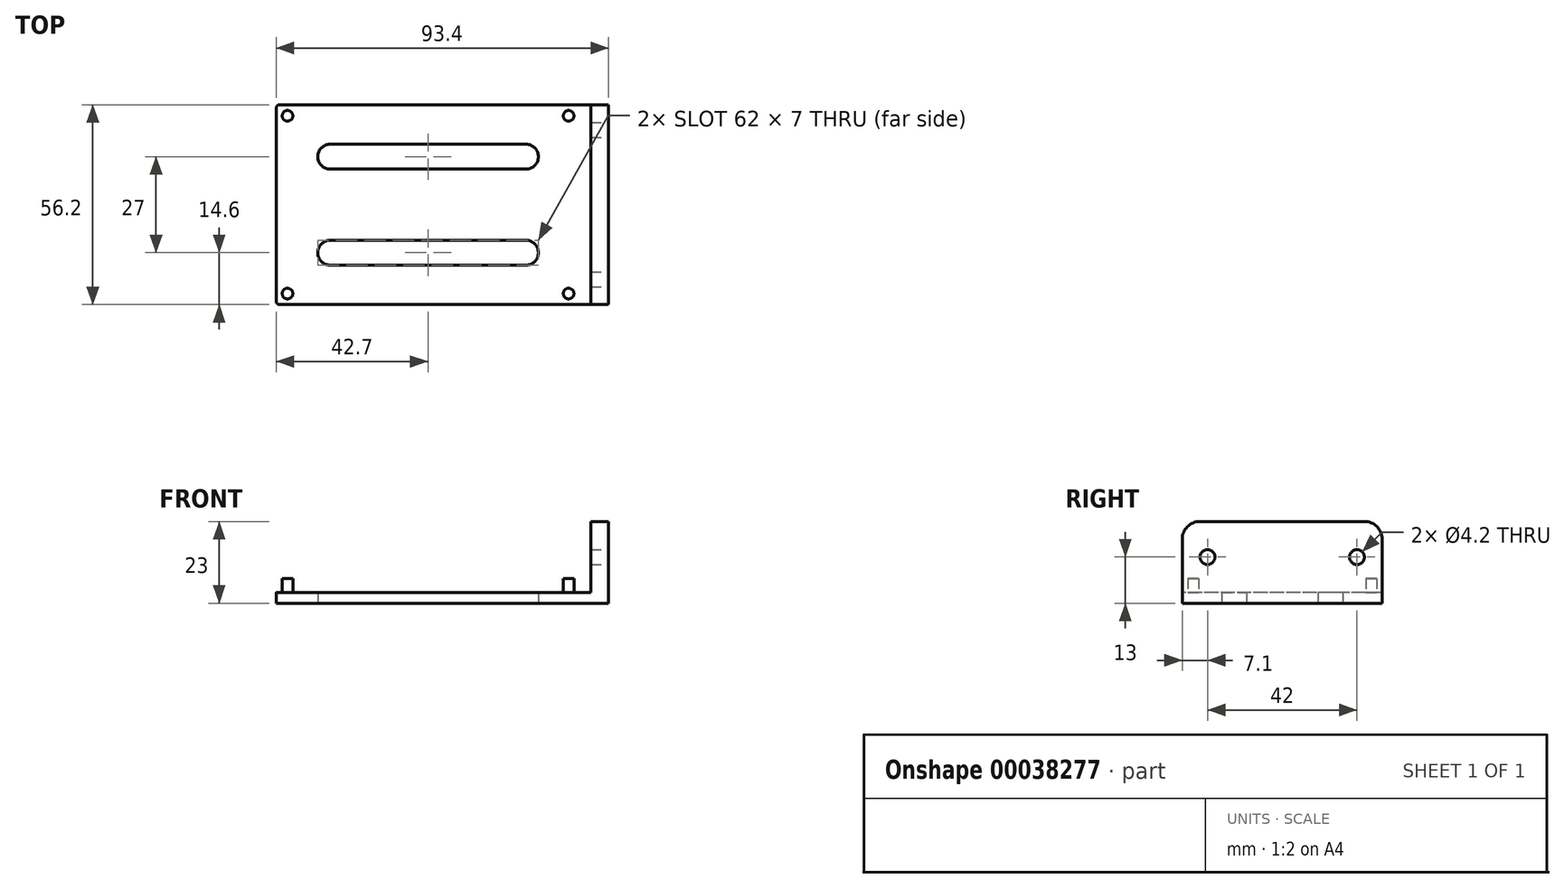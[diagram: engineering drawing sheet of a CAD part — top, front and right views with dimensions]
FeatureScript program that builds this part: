
annotation { "Feature Type Name" : "Feature", "Feature Type Description" : "" }
export const myFeature = defineFeature(function(context is Context, id is Id, definition is map)
    precondition{}
    {
        {
            var Q0;
            Q0=qCreatedBy(makeId("Top.planeOp"),FACE);
            var sketch = newSketch(context, id + "F0", { "sketchPlane" : qUnion([Q0])});
            skArc(sketch, "E0", {"start": v(-41.7, 28.1) * mm, "mid": v(-42.4, 27.8) * mm, "end": v(-42.7, 27.1) * mm});
            skLineSegment(sketch, "E1", {"start": v(-42.7, 27.1) * mm, "end": v(-42.7, -27.1) * mm});
            skArc(sketch, "E2", {"start": v(42.7, 27.1) * mm, "mid": v(42.4, 27.8) * mm, "end": v(41.7, 28.1) * mm});
            skArc(sketch, "E3", {"start": v(41.7, -28.1) * mm, "mid": v(42.4, -27.8) * mm, "end": v(42.7, -27.1) * mm});
            skLineSegment(sketch, "E4", {"start": v(42.7, -27.1) * mm, "end": v(42.7, 27.1) * mm});
            skArc(sketch, "E5", {"start": v(-42.7, -27.1) * mm, "mid": v(-42.4, -27.8) * mm, "end": v(-41.7, -28.1) * mm});
            skLineSegment(sketch, "E6", {"start": v(-41.7, -28.1) * mm, "end": v(41.7, -28.1) * mm});
            skCircle(sketch, "E7", {"center": v(39.5, 25) * mm, "radius": 1.5 * mm});
            skCircle(sketch, "E8", {"center": v(39.5, -25) * mm, "radius": 1.5 * mm});
            skCircle(sketch, "E9", {"center": v(-39.5, -25) * mm, "radius": 1.5 * mm});
            skCircle(sketch, "E10", {"center": v(-39.5, 25) * mm, "radius": 1.5 * mm});
            skCircle(sketch, "E11", {"center": v(-39.5, 25) * mm, "radius": 3.1 * mm});
            skLineSegment(sketch, "E12.bottom", {"start": v(-27.5, 17) * mm, "end": v(27.5, 17) * mm});
            skLineSegment(sketch, "E12.top", {"start": v(-27.5, 10) * mm, "end": v(27.5, 10) * mm});
            skLineSegment(sketch, "E12.left", {"start": v(-27.5, 17) * mm, "end": v(-27.5, 10) * mm, "construction": true});
            skLineSegment(sketch, "E12.right", {"start": v(27.5, 17) * mm, "end": v(27.5, 10) * mm, "construction": true});
            skArc(sketch, "E13", {"start": v(-27.5, 17) * mm, "mid": v(-31, 13.5) * mm, "end": v(-27.5, 10) * mm});
            skArc(sketch, "E14", {"start": v(27.5, 10) * mm, "mid": v(31, 13.5) * mm, "end": v(27.5, 17) * mm});
            skLineSegment(sketch, "E15", {"start": v(-42.7, 0) * mm, "end": v(42.7, 0) * mm, "construction": true});
            skLineSegment(sketch, "E16.MirrorCS", {"start": v(-27.5, -17) * mm, "end": v(-27.5, -10) * mm});
            skLineSegment(sketch, "E17.MirrorCS", {"start": v(27.5, -17) * mm, "end": v(27.5, -10) * mm});
            skArc(sketch, "E18.MirrorCS", {"start": v(27.5, -10) * mm, "mid": v(31, -13.5) * mm, "end": v(27.5, -17) * mm});
            skLineSegment(sketch, "E19.MirrorCS", {"start": v(-27.5, -10) * mm, "end": v(27.5, -10) * mm});
            skLineSegment(sketch, "E20.MirrorCS", {"start": v(-27.5, -17) * mm, "end": v(27.5, -17) * mm});
            skArc(sketch, "E21.MirrorCS", {"start": v(-27.5, -17) * mm, "mid": v(-31, -13.5) * mm, "end": v(-27.5, -10) * mm});
            skLineSegment(sketch, "E22", {"start": v(0, 17) * mm, "end": v(0, 10) * mm, "construction": true});
            skCircle(sketch, "E23.MirrorC", {"center": v(-39.5, -25) * mm, "radius": 3.1 * mm});
            skCircle(sketch, "E24.MirrorC", {"center": v(39.5, 25) * mm, "radius": 3.1 * mm});
            skCircle(sketch, "E25.MirrorC", {"center": v(39.5, -25) * mm, "radius": 3.1 * mm});
            skLineSegment(sketch, "E26", {"start": v(41.7, 28.1) * mm, "end": v(-41.7, 28.1) * mm});
            skLineSegment(sketch, "E27.bottom", {"start": v(41.7, 28.1) * mm, "end": v(50.7, 28.1) * mm});
            skLineSegment(sketch, "E27.top", {"start": v(41.7, -28.1) * mm, "end": v(50.7, -28.1) * mm});
            skLineSegment(sketch, "E27.left", {"start": v(41.7, 28.1) * mm, "end": v(41.7, -28.1) * mm, "construction": true});
            skLineSegment(sketch, "E27.right", {"start": v(50.7, 28.1) * mm, "end": v(50.7, -28.1) * mm});
            skLineSegment(sketch, "E28", {"start": v(45.7, 28.1) * mm, "end": v(45.7, -28.1) * mm});
            skSolve(sketch);
        }
        {
            var Q0;
            Q0=makeQuery(id+"F0.imprint","IMPRINT",FACE,{"disambiguationData":[TD([[makeQuery(id+"F0.imprint","IMPRINT",EDGE,{"derivedFrom":sQuery(id+"F0.wireOp",EDGE,"E10")}),-1.0]])]});
            var Q1;
            Q1=makeQuery(id+"F0.imprint","IMPRINT",FACE,{"disambiguationData":[TD([[makeQuery(id+"F0.imprint","IMPRINT",EDGE,{"derivedFrom":sQuery(id+"F0.wireOp",EDGE,"E10")}),1.0]])]});
            var Q2;
            Q2=makeQuery(id+"F0.imprint","IMPRINT",FACE,{"disambiguationData":[TD([[makeQuery(id+"F0.imprint","IMPRINT",EDGE,{"derivedFrom":sQuery(id+"F0.wireOp",EDGE,"E0")}),1.0]])]});
            var Q3;
            Q3=makeQuery(id+"F0.imprint","IMPRINT",FACE,{"disambiguationData":[TD([[makeQuery(id+"F0.imprint","IMPRINT",EDGE,{"derivedFrom":sQuery(id+"F0.wireOp",EDGE,"E9")}),-1.0]])]});
            var Q4;
            Q4=makeQuery(id+"F0.imprint","IMPRINT",FACE,{"disambiguationData":[TD([[makeQuery(id+"F0.imprint","IMPRINT",EDGE,{"derivedFrom":sQuery(id+"F0.wireOp",EDGE,"E9")}),1.0]])]});
            var Q5;
            Q5=makeQuery(id+"F0.imprint","IMPRINT",FACE,{"disambiguationData":[TD([[makeQuery(id+"F0.imprint","IMPRINT",EDGE,{"derivedFrom":sQuery(id+"F0.wireOp",EDGE,"E8")}),-1.0]])]});
            var Q6;
            Q6=makeQuery(id+"F0.imprint","IMPRINT",FACE,{"disambiguationData":[TD([[makeQuery(id+"F0.imprint","IMPRINT",EDGE,{"derivedFrom":sQuery(id+"F0.wireOp",EDGE,"E8")}),1.0]])]});
            var Q7;
            Q7=makeQuery(id+"F0.imprint","IMPRINT",FACE,{"disambiguationData":[TD([[makeQuery(id+"F0.imprint","IMPRINT",EDGE,{"derivedFrom":sQuery(id+"F0.wireOp",EDGE,"E7")}),-1.0]])]});
            var Q8;
            Q8=makeQuery(id+"F0.imprint","IMPRINT",FACE,{"disambiguationData":[TD([[makeQuery(id+"F0.imprint","IMPRINT",EDGE,{"derivedFrom":sQuery(id+"F0.wireOp",EDGE,"E7")}),1.0]])]});
            var Q9;
            {var subQ3=sQuery(id+"F0.wireOp",EDGE,"E2");Q9=makeQuery(id+"F0.imprint","IMPRINT",FACE,{"disambiguationData":[TD([[makeQuery(id+"F0.imprint","IMPRINT",EDGE,{"derivedFrom":subQ3}),-1.0]])]});}
            extrude(context, id + "F1", {"entities" : qUnion([Q0, Q1, Q2, Q3, Q4, Q5, Q6, Q7, Q8, Q9]), "depth" : 3 * mm});
        }
        {
            var Q0;
            Q0=makeQuery(id+"F0.imprint","IMPRINT",FACE,{"disambiguationData":[TD([[makeQuery(id+"F0.imprint","IMPRINT",EDGE,{"derivedFrom":sQuery(id+"F0.wireOp",EDGE,"E10")}),1.0]])]});
            var Q1;
            Q1=makeQuery(id+"F0.imprint","IMPRINT",FACE,{"disambiguationData":[TD([[makeQuery(id+"F0.imprint","IMPRINT",EDGE,{"derivedFrom":sQuery(id+"F0.wireOp",EDGE,"E9")}),1.0]])]});
            var Q2;
            Q2=makeQuery(id+"F0.imprint","IMPRINT",FACE,{"disambiguationData":[TD([[makeQuery(id+"F0.imprint","IMPRINT",EDGE,{"derivedFrom":sQuery(id+"F0.wireOp",EDGE,"E8")}),1.0]])]});
            var Q3;
            Q3=makeQuery(id+"F0.imprint","IMPRINT",FACE,{"disambiguationData":[TD([[makeQuery(id+"F0.imprint","IMPRINT",EDGE,{"derivedFrom":sQuery(id+"F0.wireOp",EDGE,"E7")}),1.0]])]});
            extrude(context, id + "F2", {"entities" : qUnion([Q0, Q1, Q2, Q3]), "operationType" : NewBodyOperationType.ADD, "depth" : 7 * mm});
        }
        {
            var Q0;
            {var subQ1=sQuery(id+"F0.wireOp",EDGE,"E27.right");Q0=makeQuery(id+"F0.imprint","IMPRINT",FACE,{"disambiguationData":[TD([[makeQuery(id+"F0.imprint","IMPRINT",EDGE,{"derivedFrom":subQ1}),-1.0]])]});}
            extrude(context, id + "F3", {"entities" : qUnion([Q0]), "operationType" : NewBodyOperationType.ADD, "depth" : 23 * mm});
        }
        {
            var Q0;
            Q0=makeQuery(id+"F3.opExtrude","SWEPT_FACE",FACE,{"disambiguationData":[OSD([sQuery(id+"F0.wireOp",EDGE,"E27.right")])]});
            var sketch = newSketch(context, id + "F4", { "sketchPlane" : qUnion([Q0])});
            skLineSegment(sketch, "E29.0", {"start": v(28.1, 23) * mm, "end": v(-28.1, 23) * mm});
            skLineSegment(sketch, "E29.2", {"start": v(-28.1, 23) * mm, "end": v(-28.1, 0) * mm});
            skLineSegment(sketch, "E29.3", {"start": v(28.1, 23) * mm, "end": v(28.1, 0) * mm});
            skCircle(sketch, "E30", {"center": v(-21, 13) * mm, "radius": 2.1 * mm});
            skCircle(sketch, "E31", {"center": v(21, 13) * mm, "radius": 2.1 * mm});
            skLineSegment(sketch, "E32", {"start": v(0, 23) * mm, "end": v(0, 3) * mm, "construction": true});
            skLineSegment(sketch, "E33.0", {"start": v(28.1, 3) * mm, "end": v(-28.1, 3) * mm});
            skPoint(sketch, "E34", {"position": v(0, 13) * mm});
            skSolve(sketch);
        }
        {
            var Q0;
            Q0=makeQuery(id+"F4.imprint","IMPRINT",FACE,{"disambiguationData":[TD([[makeQuery(id+"F4.imprint","IMPRINT",EDGE,{"derivedFrom":sQuery(id+"F4.wireOp",EDGE,"E30")}),1.0]])]});
            var Q1;
            Q1=makeQuery(id+"F4.imprint","IMPRINT",FACE,{"disambiguationData":[TD([[makeQuery(id+"F4.imprint","IMPRINT",EDGE,{"derivedFrom":sQuery(id+"F4.wireOp",EDGE,"E31")}),1.0]])]});
            var Q2;
            Q2=makeQuery(id+"F3.opExtrude","SWEPT_FACE",FACE,{"disambiguationData":[OSD([sQuery(id+"F0.wireOp",EDGE,"E28")])]});
            extrude(context, id + "F5", {"entities" : qUnion([Q0, Q1]), "operationType" : NewBodyOperationType.REMOVE, "endBound" : BoundingType.UP_TO_SURFACE, "oppositeDirection" : true, "endBoundEntityFace" : qUnion([Q2]), "depth" : 25 * mm});
        }
        {
            var Q0;
            Q0=makeQuery(id+"F3.opExtrude","CAP_EDGE",EDGE,{"disambiguationData":[OSD([sQuery(id+"F0.wireOp",EDGE,"E27.bottom")])],"isStart":false});
            var Q1;
            Q1=makeQuery(id+"F3.opExtrude","CAP_EDGE",EDGE,{"disambiguationData":[OSD([sQuery(id+"F0.wireOp",EDGE,"E27.top")])],"isStart":false});
            fillet(context, id + "F6", {"entities" : qUnion([Q0, Q1]), "radius" : 5 * mm, "tangentPropagation" : true, "allowEdgeOverflow" : false});
        }
    });
